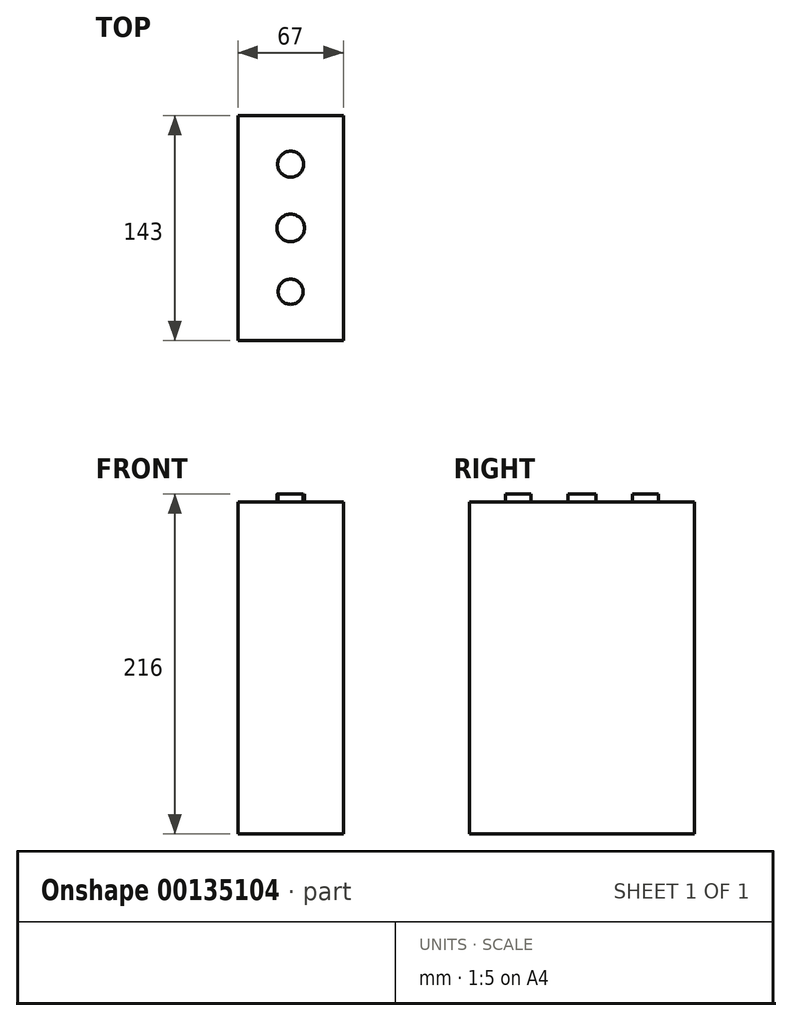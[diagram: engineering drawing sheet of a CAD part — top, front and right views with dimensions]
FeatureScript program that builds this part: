
annotation { "Feature Type Name" : "Feature", "Feature Type Description" : "" }
export const myFeature = defineFeature(function(context is Context, id is Id, definition is map)
    precondition{}
    {
        {
            var Q0;
            Q0=qCreatedBy(makeId("Front.planeOp"),FACE);
            var sketch = newSketch(context, id + "F0", { "sketchPlane" : qUnion([Q0])});
            skLineSegment(sketch, "E0.bottom", {"start": v(-38.13, 162.47) * mm, "end": v(28.87, 162.47) * mm});
            skLineSegment(sketch, "E0.top", {"start": v(-38.13, -53.53) * mm, "end": v(28.87, -53.53) * mm});
            skLineSegment(sketch, "E0.left", {"start": v(-38.13, 162.47) * mm, "end": v(-38.13, -53.53) * mm});
            skLineSegment(sketch, "E0.right", {"start": v(28.87, 162.47) * mm, "end": v(28.87, -53.53) * mm});
            skSolve(sketch);
        }
        {
            var Q0;
            Q0=makeQuery(id+"F0.imprint","IMPRINT",FACE,{"disambiguationData":[TD([[makeQuery(id+"F0.imprint","IMPRINT",EDGE,{"derivedFrom":sQuery(id+"F0.wireOp",EDGE,"E0.bottom")}),-1.0]])]});
            extrude(context, id + "F1", {"entities" : qUnion([Q0]), "depth" : 143 * mm});
        }
        {
            var Q0;
            Q0=makeQuery(id+"F1.opExtrude","SWEPT_FACE",FACE,{"disambiguationData":[OSD([sQuery(id+"F0.wireOp",EDGE,"E0.bottom")])]});
            var sketch = newSketch(context, id + "F2", { "sketchPlane" : qUnion([Q0])});
            skLineSegment(sketch, "E1", {"start": v(-4.63, -31) * mm, "end": v(-4.63, -112) * mm});
            skPoint(sketch, "E1.startSnap0", {"position": v(-4.63, 0) * mm});
            skCircle(sketch, "E2", {"center": v(-4.63, -31) * mm, "radius": 8.25 * mm});
            skCircle(sketch, "E3", {"center": v(-4.63, -112) * mm, "radius": 8 * mm});
            skCircle(sketch, "E4", {"center": v(-4.63, -71.5) * mm, "radius": 8.78 * mm});
            skSolve(sketch);
        }
        {
            var Q0;
            Q0=makeQuery(id+"F2.imprint","IMPRINT",FACE,{"disambiguationData":[TD([[makeQuery(id+"F2.imprint","IMPRINT",EDGE,{"derivedFrom":sQuery(id+"F2.wireOp",EDGE,"E2")}),-1.0]])]});
            extrude(context, id + "F3", {"entities" : qUnion([Q0]), "operationType" : NewBodyOperationType.REMOVE, "oppositeDirection" : true, "depth" : 5 * mm});
        }
    });
